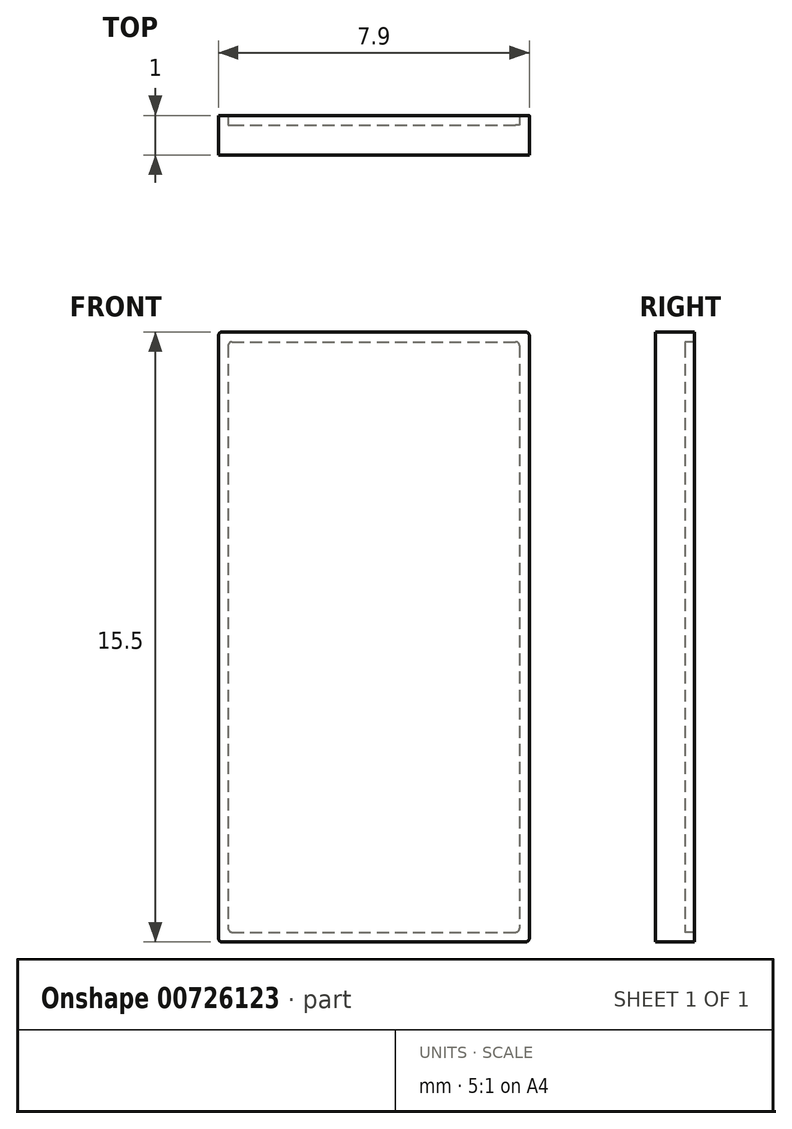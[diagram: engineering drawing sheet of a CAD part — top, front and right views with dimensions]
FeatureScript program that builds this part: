
annotation { "Feature Type Name" : "Feature", "Feature Type Description" : "" }
export const myFeature = defineFeature(function(context is Context, id is Id, definition is map)
    precondition{}
    {
        {
            var Q0;
            Q0=qCreatedBy(makeId("Front.planeOp"),FACE);
            var sketch = newSketch(context, id + "F0", { "sketchPlane" : qUnion([Q0])});
            skLineSegment(sketch, "E0.bottom", {"start": v(-3.6, 7.5) * mm, "end": v(3.6, 7.5) * mm});
            skLineSegment(sketch, "E0.top", {"start": v(-3.6, -7.5) * mm, "end": v(3.6, -7.5) * mm});
            skLineSegment(sketch, "E0.left", {"start": v(-3.7, 7.4) * mm, "end": v(-3.7, -7.4) * mm});
            skLineSegment(sketch, "E0.right", {"start": v(3.7, 7.4) * mm, "end": v(3.7, -7.4) * mm});
            skPoint(sketch, "E0.middle", {"position": v(0, 0) * mm});
            skLineSegment(sketch, "E1.0", {"start": v(-3.85, 7.75) * mm, "end": v(3.85, 7.75) * mm});
            skLineSegment(sketch, "E1.1", {"start": v(-3.95, 7.65) * mm, "end": v(-3.95, -7.65) * mm});
            skLineSegment(sketch, "E1.2", {"start": v(-3.85, -7.75) * mm, "end": v(3.85, -7.75) * mm});
            skLineSegment(sketch, "E1.3", {"start": v(3.95, 7.65) * mm, "end": v(3.95, -7.65) * mm});
            skPoint(sketch, "E2.visualSharp", {"position": v(3.95, 7.75) * mm});
            skArc(sketch, "E2.filletArc", {"start": v(3.95, 7.65) * mm, "mid": v(3.92, 7.72) * mm, "end": v(3.85, 7.75) * mm});
            skPoint(sketch, "E3.visualSharp", {"position": v(-3.95, 7.75) * mm});
            skArc(sketch, "E3.filletArc", {"start": v(-3.85, 7.75) * mm, "mid": v(-3.92, 7.72) * mm, "end": v(-3.95, 7.65) * mm});
            skPoint(sketch, "E4.visualSharp", {"position": v(-3.95, -7.75) * mm});
            skArc(sketch, "E4.filletArc", {"start": v(-3.95, -7.65) * mm, "mid": v(-3.92, -7.72) * mm, "end": v(-3.85, -7.75) * mm});
            skPoint(sketch, "E5.visualSharp", {"position": v(3.95, -7.75) * mm});
            skArc(sketch, "E5.filletArc", {"start": v(3.85, -7.75) * mm, "mid": v(3.92, -7.72) * mm, "end": v(3.95, -7.65) * mm});
            skPoint(sketch, "E6.visualSharp", {"position": v(3.7, -7.5) * mm});
            skArc(sketch, "E6.filletArc", {"start": v(3.6, -7.5) * mm, "mid": v(3.67, -7.47) * mm, "end": v(3.7, -7.4) * mm});
            skPoint(sketch, "E7.visualSharp", {"position": v(-3.7, -7.5) * mm});
            skArc(sketch, "E7.filletArc", {"start": v(-3.7, -7.4) * mm, "mid": v(-3.67, -7.47) * mm, "end": v(-3.6, -7.5) * mm});
            skPoint(sketch, "E8.visualSharp", {"position": v(-3.7, 7.5) * mm});
            skArc(sketch, "E8.filletArc", {"start": v(-3.6, 7.5) * mm, "mid": v(-3.67, 7.47) * mm, "end": v(-3.7, 7.4) * mm});
            skPoint(sketch, "E9.visualSharp", {"position": v(3.7, 7.5) * mm});
            skArc(sketch, "E9.filletArc", {"start": v(3.7, 7.4) * mm, "mid": v(3.67, 7.47) * mm, "end": v(3.6, 7.5) * mm});
            skSolve(sketch);
        }
        {
            var Q0;
            Q0=makeQuery(id+"F0.imprint","IMPRINT",FACE,{"disambiguationData":[TD([[makeQuery(id+"F0.imprint","IMPRINT",EDGE,{"derivedFrom":sQuery(id+"F0.wireOp",EDGE,"E0.bottom")}),-1.0]])]});
            var Q1;
            Q1=makeQuery(id+"F0.imprint","IMPRINT",FACE,{"disambiguationData":[TD([[makeQuery(id+"F0.imprint","IMPRINT",EDGE,{"derivedFrom":sQuery(id+"F0.wireOp",EDGE,"E0.bottom")}),1.0]])]});
            extrude(context, id + "F1", {"entities" : qUnion([Q0, Q1]), "depth" : .75 * mm, "offsetDistance" : 25 * mm});
        }
        {
            var Q0;
            Q0=makeQuery(id+"F0.imprint","IMPRINT",FACE,{"disambiguationData":[TD([[makeQuery(id+"F0.imprint","IMPRINT",EDGE,{"derivedFrom":sQuery(id+"F0.wireOp",EDGE,"E1.0")}),-1.0]])]});
            extrude(context, id + "F2", {"entities" : qUnion([Q0]), "operationType" : NewBodyOperationType.ADD, "depth" : .75 * mm, "offsetDistance" : 25 * mm});
        }
        {
            var Q0;
            Q0 = qSketchRegion(id + "F0", true);
            extrude(context, id + "F3", {"entities" : qUnion([Q0]), "operationType" : NewBodyOperationType.ADD, "oppositeDirection" : true, "depth" : .25 * mm, "offsetDistance" : 25 * mm});
        }
    });
